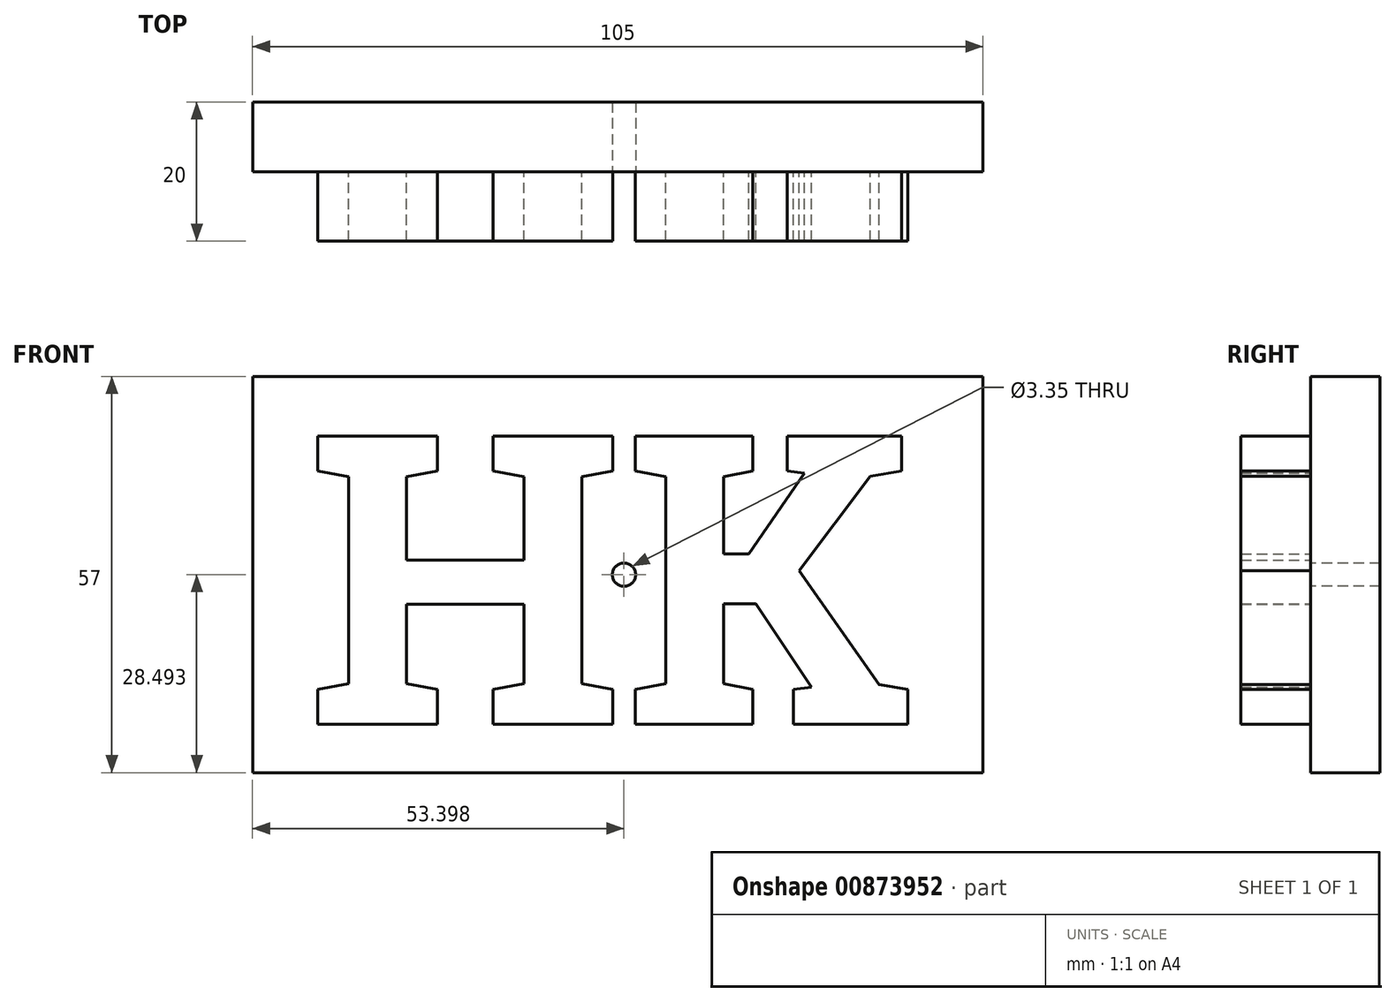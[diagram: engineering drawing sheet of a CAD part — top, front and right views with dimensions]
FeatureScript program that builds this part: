
annotation { "Feature Type Name" : "Feature", "Feature Type Description" : "" }
export const myFeature = defineFeature(function(context is Context, id is Id, definition is map)
    precondition{}
    {
        {
            var Q0;
            Q0=qCreatedBy(makeId("Front.planeOp"),FACE);
            var sketch = newSketch(context, id + "F0", { "sketchPlane" : qUnion([Q0])});
            skText(sketch, "E0", { "text": "HK", "fontName": "RobotoSlab-Bold.ttf"});
            const initialGuessF0  = {"E0": [-0.03826, -0.02312, 1, 0, 0.042]};
            skSetInitialGuess(sketch, initialGuessF0);
            skSolve(sketch);
        }
        {
            var Q0;
            Q0 = qSketchRegion(id + "F0", true);
            extrude(context, id + "F1", {"entities" : qUnion([Q0]), "depth" : 10 * mm, "offsetDistance" : 25 * mm});
        }
        {
            var Q0;
            Q0=makeQuery(id+"F1.opExtrude","CAP_FACE",FACE,{"disambiguationData":[OSD([sQuery(id+"F0.wireOp",EDGE,"E0.sketch_text.stroke-0"),sQuery(id+"F0.wireOp",EDGE,"E0.sketch_text.stroke-1"),sQuery(id+"F0.wireOp",EDGE,"E0.sketch_text.stroke-2"),sQuery(id+"F0.wireOp",EDGE,"E0.sketch_text.stroke-3"),sQuery(id+"F0.wireOp",EDGE,"E0.sketch_text.stroke-4"),sQuery(id+"F0.wireOp",EDGE,"E0.sketch_text.stroke-5"),sQuery(id+"F0.wireOp",EDGE,"E0.sketch_text.stroke-6"),sQuery(id+"F0.wireOp",EDGE,"E0.sketch_text.stroke-7"),sQuery(id+"F0.wireOp",EDGE,"E0.sketch_text.stroke-8"),sQuery(id+"F0.wireOp",EDGE,"E0.sketch_text.stroke-9"),sQuery(id+"F0.wireOp",EDGE,"E0.sketch_text.stroke-10"),sQuery(id+"F0.wireOp",EDGE,"E0.sketch_text.stroke-11"),sQuery(id+"F0.wireOp",EDGE,"E0.sketch_text.stroke-12"),sQuery(id+"F0.wireOp",EDGE,"E0.sketch_text.stroke-13"),sQuery(id+"F0.wireOp",EDGE,"E0.sketch_text.stroke-14"),sQuery(id+"F0.wireOp",EDGE,"E0.sketch_text.stroke-15"),sQuery(id+"F0.wireOp",EDGE,"E0.sketch_text.stroke-16"),sQuery(id+"F0.wireOp",EDGE,"E0.sketch_text.stroke-17"),sQuery(id+"F0.wireOp",EDGE,"E0.sketch_text.stroke-18"),sQuery(id+"F0.wireOp",EDGE,"E0.sketch_text.stroke-19"),sQuery(id+"F0.wireOp",EDGE,"E0.sketch_text.stroke-20"),sQuery(id+"F0.wireOp",EDGE,"E0.sketch_text.stroke-21"),sQuery(id+"F0.wireOp",EDGE,"E0.sketch_text.stroke-22"),sQuery(id+"F0.wireOp",EDGE,"E0.sketch_text.stroke-23"),sQuery(id+"F0.wireOp",EDGE,"E0.sketch_text.stroke-24"),sQuery(id+"F0.wireOp",EDGE,"E0.sketch_text.stroke-25"),sQuery(id+"F0.wireOp",EDGE,"E0.sketch_text.stroke-26"),sQuery(id+"F0.wireOp",EDGE,"E0.sketch_text.stroke-27"),sQuery(id+"F0.wireOp",EDGE,"E0.sketch_text.stroke-28"),sQuery(id+"F0.wireOp",EDGE,"E0.sketch_text.stroke-29")])],"isStart":true});
            var sketch = newSketch(context, id + "F2", { "sketchPlane" : qUnion([Q0])});
            skLineSegment(sketch, "E1.bottom", {"start": v(46.06, 26.9) * mm, "end": v(-58.94, 26.9) * mm});
            skLineSegment(sketch, "E1.top", {"start": v(46.06, -30.1) * mm, "end": v(-58.94, -30.1) * mm});
            skLineSegment(sketch, "E1.left", {"start": v(46.06, 26.9) * mm, "end": v(46.06, -30.1) * mm});
            skLineSegment(sketch, "E1.right", {"start": v(-58.94, 26.9) * mm, "end": v(-58.94, -30.1) * mm});
            skCircle(sketch, "E2", {"center": v(-7.34, -1.6) * mm, "radius": 1.68 * mm});
            skSolve(sketch);
        }
        {
            var Q0;
            Q0 = qSketchRegion(id + "F2", true);
            extrude(context, id + "F3", {"entities" : qUnion([Q0]), "operationType" : NewBodyOperationType.ADD, "depth" : 10 * mm, "offsetDistance" : 25 * mm});
        }
    });
